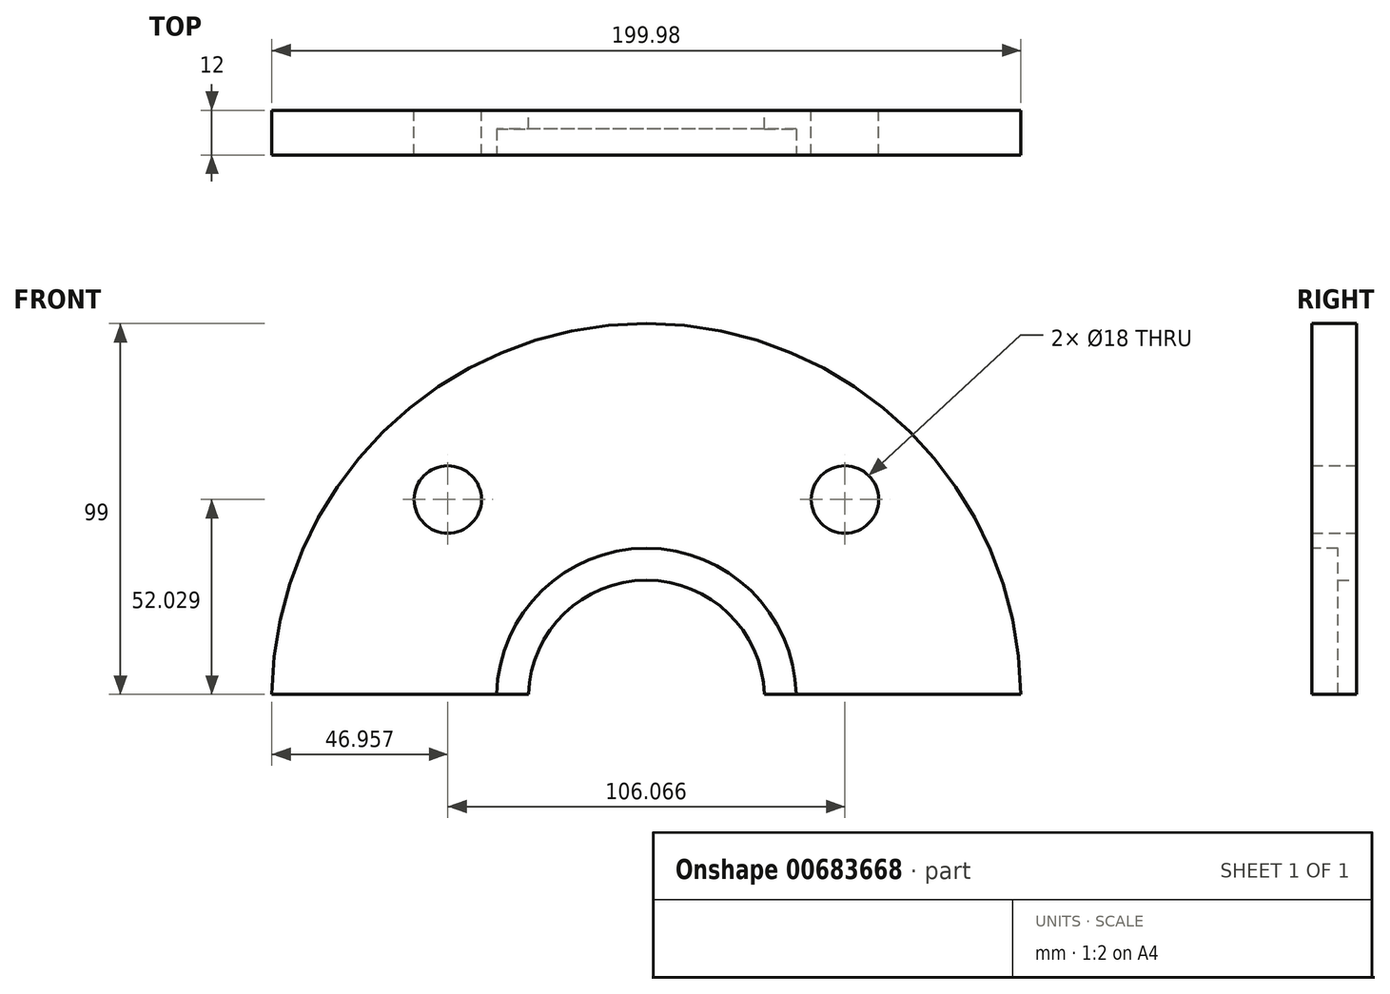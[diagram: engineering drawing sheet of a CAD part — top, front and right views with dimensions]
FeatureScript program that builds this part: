
annotation { "Feature Type Name" : "Feature", "Feature Type Description" : "" }
export const myFeature = defineFeature(function(context is Context, id is Id, definition is map)
    precondition{}
    {
        {
            var Q0;
            Q0=qCreatedBy(makeId("Front.planeOp"),FACE);
            var sketch = newSketch(context, id + "F0", { "sketchPlane" : qUnion([Q0])});
            skLineSegment(sketch, "E0.0", {"start": v(-100, -1.71) * mm, "end": v(-31.48, -1.71) * mm});
            skArc(sketch, "E1.trimOffspring", {"start": v(100, -1.71) * mm, "mid": v(0, 97.29) * mm, "end": v(-100, -1.71) * mm});
            skLineSegment(sketch, "E2", {"start": v(0, -2.71) * mm, "end": v(-53.03, 50.32) * mm});
            skCircle(sketch, "E3", {"center": v(-53.03, 50.32) * mm, "radius": 9 * mm});
            skCircle(sketch, "E4.MirrorC", {"center": v(53.03, 50.32) * mm, "radius": 9 * mm});
            skArc(sketch, "E5", {"start": v(31.48, -1.71) * mm, "mid": v(0, 28.79) * mm, "end": v(-31.48, -1.71) * mm});
            skLineSegment(sketch, "E6.trimOffspring", {"start": v(31.48, -1.71) * mm, "end": v(100, -1.71) * mm});
            skSolve(sketch);
        }
        {
            var Q0;
            {var subQ0=sQuery(id+"F0.wireOp",EDGE,"E0.0");Q0=makeQuery(id+"F0.imprint","IMPRINT",FACE,{"disambiguationData":[TD([[makeQuery(id+"F0.imprint","IMPRINT",EDGE,{"derivedFrom":subQ0}),1.0]])]});}
            extrude(context, id + "F1", {"entities" : qUnion([Q0]), "depth" : 12 * mm, "offsetDistance" : 25 * mm});
        }
        {
            var Q0;
            Q0=makeQuery(id+"F1.opExtrude","CAP_FACE",FACE,{"disambiguationData":[OSD([sQuery(id+"F0.wireOp",EDGE,"E0.0"),sQuery(id+"F0.wireOp",EDGE,"E1.trimOffspring"),sQuery(id+"F0.wireOp",EDGE,"E3"),sQuery(id+"F0.wireOp",EDGE,"E4.MirrorC"),sQuery(id+"F0.wireOp",EDGE,"E5"),sQuery(id+"F0.wireOp",EDGE,"E6.trimOffspring")])],"isStart":false});
            var sketch = newSketch(context, id + "F2", { "sketchPlane" : qUnion([Q0])});
            skCircle(sketch, "E7", {"center": v(0, -2.71) * mm, "radius": 40 * mm});
            skSolve(sketch);
        }
        {
            var Q0;
            {var subQ5=makeQuery(id+"F1.opExtrude","CAP_EDGE",EDGE,{"disambiguationData":[OSD([sQuery(id+"F0.wireOp",EDGE,"E5")])],"isStart":false});Q0=makeQuery(id+"F2.imprint","IMPRINT",FACE,{"disambiguationData":[TD([[makeQuery(id+"F2.imprint","IMPRINT",EDGE,{"derivedFrom":subQ5}),-1.0]])]});}
            extrude(context, id + "F3", {"entities" : qUnion([Q0]), "operationType" : NewBodyOperationType.REMOVE, "oppositeDirection" : true, "depth" : 7 * mm, "offsetDistance" : 25 * mm});
        }
    });
